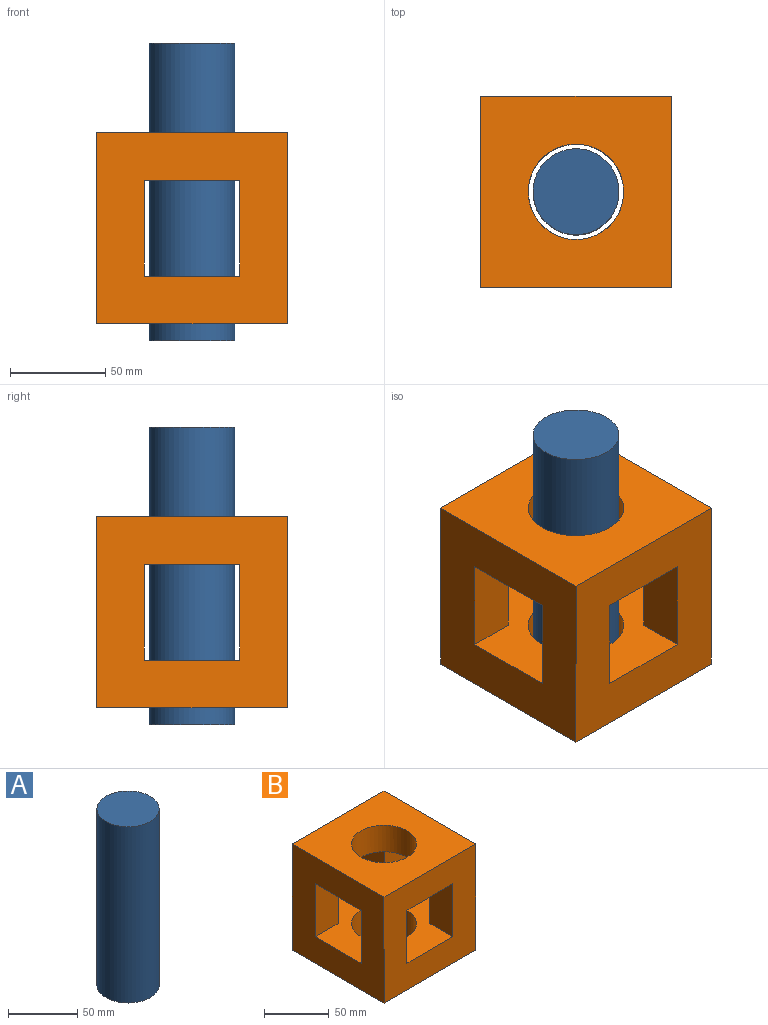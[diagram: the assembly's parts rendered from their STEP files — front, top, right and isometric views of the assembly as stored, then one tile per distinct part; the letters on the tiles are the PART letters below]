
ASSEMBLY  parts=2 mates=1
PART A: 3 faces, bbox 45x45x156 mm
  f0: cylinder r=22.5mm len=156mm, axis (0,0,-1), area 22054mm2, adj f1,f2
  f1: plane 45x45mm, normal (0,0,1), area 1590.4mm2, adj f0
  f2: plane 45x45mm, normal (0,0,-1), area 1590.4mm2, adj f0
PART B: 18 faces, bbox 100x100x100 mm
  f0: plane 100x100mm, normal (-1,0,0), area 7500mm2, adj f4,f5,f6,f7,f8,f10,f14,f15
  f1: plane 100x100mm, normal (1,0,0), area 7500mm2, adj f4,f5,f6,f7,f8,f10,f12,f13
  f2: plane 50x25mm, normal (1,0,0), area 1250mm2, adj f4,f8,f10,f15
  f3: plane 50x25mm, normal (-1,0,0), area 1250mm2, adj f4,f8,f10,f13
  f4: plane 100x100mm, normal (0,1,0), area 7500mm2, adj f0,f1,f2,f3,f6,f7,f8,f10
  f5: plane 100x100mm, normal (0,-1,0), area 7500mm2, adj f0,f1,f6,f7,f8,f9,f10,f11
  f6: plane 100x100mm, normal (0,0,-1), area 8036.5mm2, adj f0,f1,f4,f5,f16
  f7: plane 100x100mm, normal (0,0,1), area 8036.5mm2, adj f0,f1,f4,f5,f17
  f8: plane 100x100mm, normal (0,0,-1), area 5536.5mm2, adj f0,f1,f2,f3,f4,f5,f9,f11
  f9: plane 50x25mm, normal (1,0,0), area 1250mm2, adj f5,f8,f10,f14
  f10: plane 100x100mm, normal (0,0,1), area 5536.5mm2, adj f0,f1,f2,f3,f4,f5,f9,f11
  f11: plane 50x25mm, normal (-1,0,0), area 1250mm2, adj f5,f8,f10,f12
  f12: plane 50x25mm, normal (0,1,0), area 1250mm2, adj f1,f8,f10,f11
  f13: plane 50x25mm, normal (0,-1,0), area 1250mm2, adj f1,f3,f8,f10
  f14: plane 50x25mm, normal (0,1,0), area 1250mm2, adj f0,f8,f9,f10
  f15: plane 50x25mm, normal (0,-1,0), area 1250mm2, adj f0,f2,f8,f10
  f16: cylinder r=25mm len=50mm, axis (0,0,1), area 3927mm2, adj f6,f10
  f17: cylinder r=25mm len=50mm, axis (0,0,1), area 3927mm2, adj f7,f8
PLACE A rot(axis=(0,1,0),0deg) t=(48.41,-38.66,-96.72)mm
PLACE B rot(axis=(0,1,0),0deg) t=(48.41,-38.66,12.27)mm
MATE slider A.f0 <-> B.f16  axis (0,0,-1) through (98.41,11.34,3.28)mm
